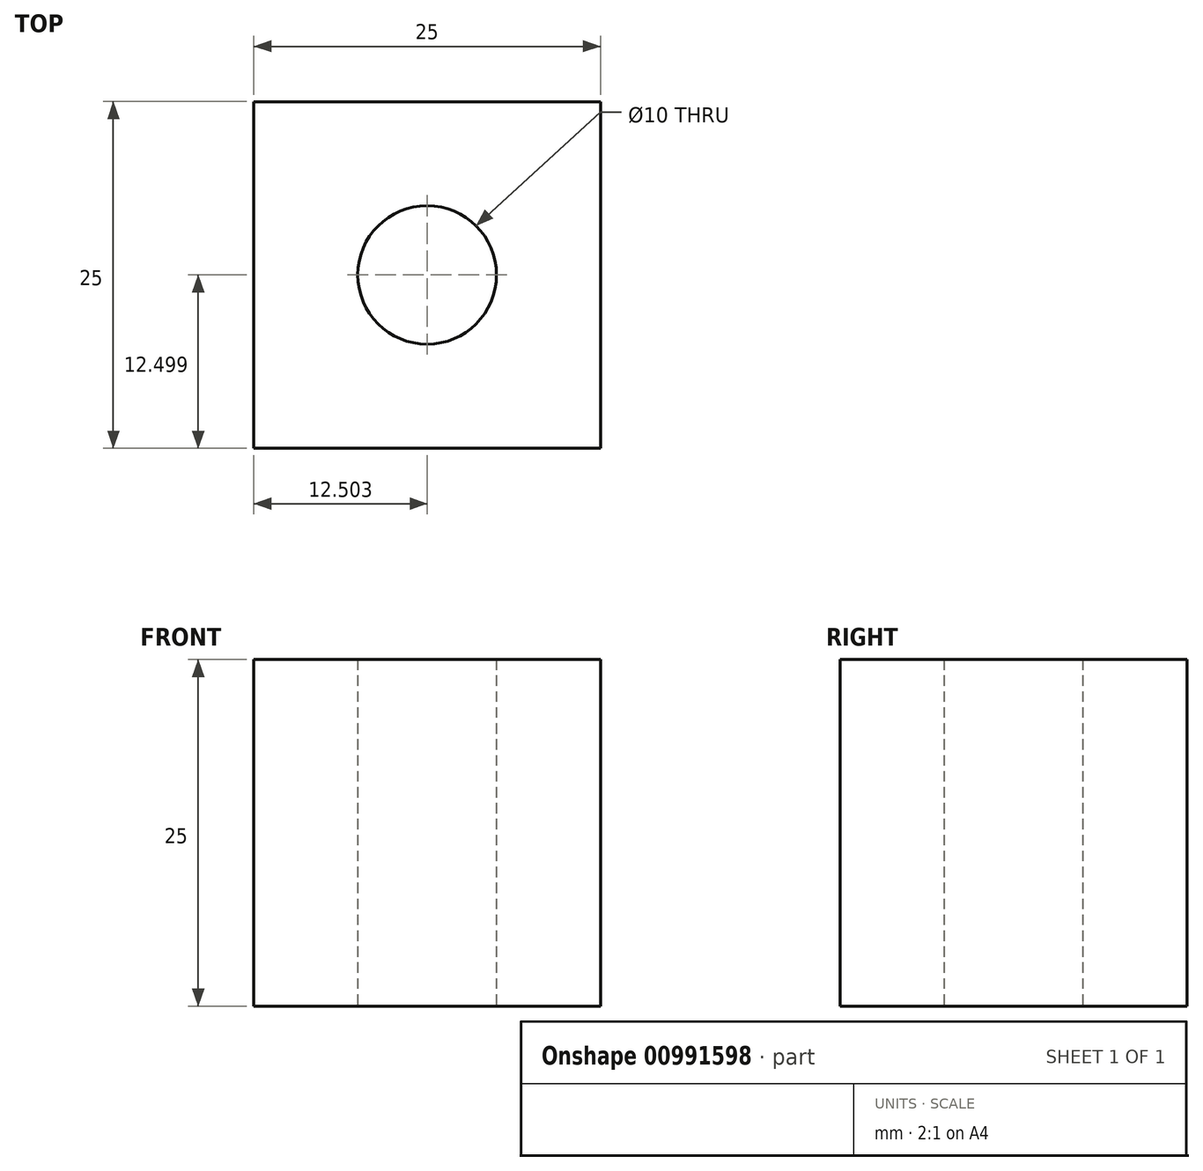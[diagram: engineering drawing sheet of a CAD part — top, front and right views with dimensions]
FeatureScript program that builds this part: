
annotation { "Feature Type Name" : "Feature", "Feature Type Description" : "" }
export const myFeature = defineFeature(function(context is Context, id is Id, definition is map)
    precondition{}
    {
        {
            var Q0;
            Q0=qCreatedBy(makeId("Top.planeOp"),FACE);
            var sketch = newSketch(context, id + "F0", { "sketchPlane" : qUnion([Q0])});
            skLineSegment(sketch, "E0.bottom", {"start": v(-1.55, 2.58) * mm, "end": v(23.45, 2.58) * mm});
            skLineSegment(sketch, "E0.top", {"start": v(-1.55, -22.42) * mm, "end": v(23.45, -22.42) * mm});
            skLineSegment(sketch, "E0.left", {"start": v(-1.55, 2.58) * mm, "end": v(-1.55, -22.42) * mm});
            skLineSegment(sketch, "E0.right", {"start": v(23.45, 2.58) * mm, "end": v(23.45, -22.42) * mm});
            skCircle(sketch, "E1", {"center": v(10.95, -9.92) * mm, "radius": 5 * mm});
            skPoint(sketch, "E1.centerSnap0", {"position": v(23.45, -9.92) * mm});
            skPoint(sketch, "E1.centerSnap1", {"position": v(10.95, 2.58) * mm});
            skSolve(sketch);
        }
        {
            var Q0;
            Q0=makeQuery(id+"F0.imprint","IMPRINT",FACE,{"disambiguationData":[TD([[makeQuery(id+"F0.imprint","IMPRINT",EDGE,{"derivedFrom":sQuery(id+"F0.wireOp",EDGE,"E0.bottom")}),-1.0]])]});
            extrude(context, id + "F1", {"entities" : qUnion([Q0]), "depth" : 25 * mm, "offsetDistance" : 25 * mm});
        }
    });
